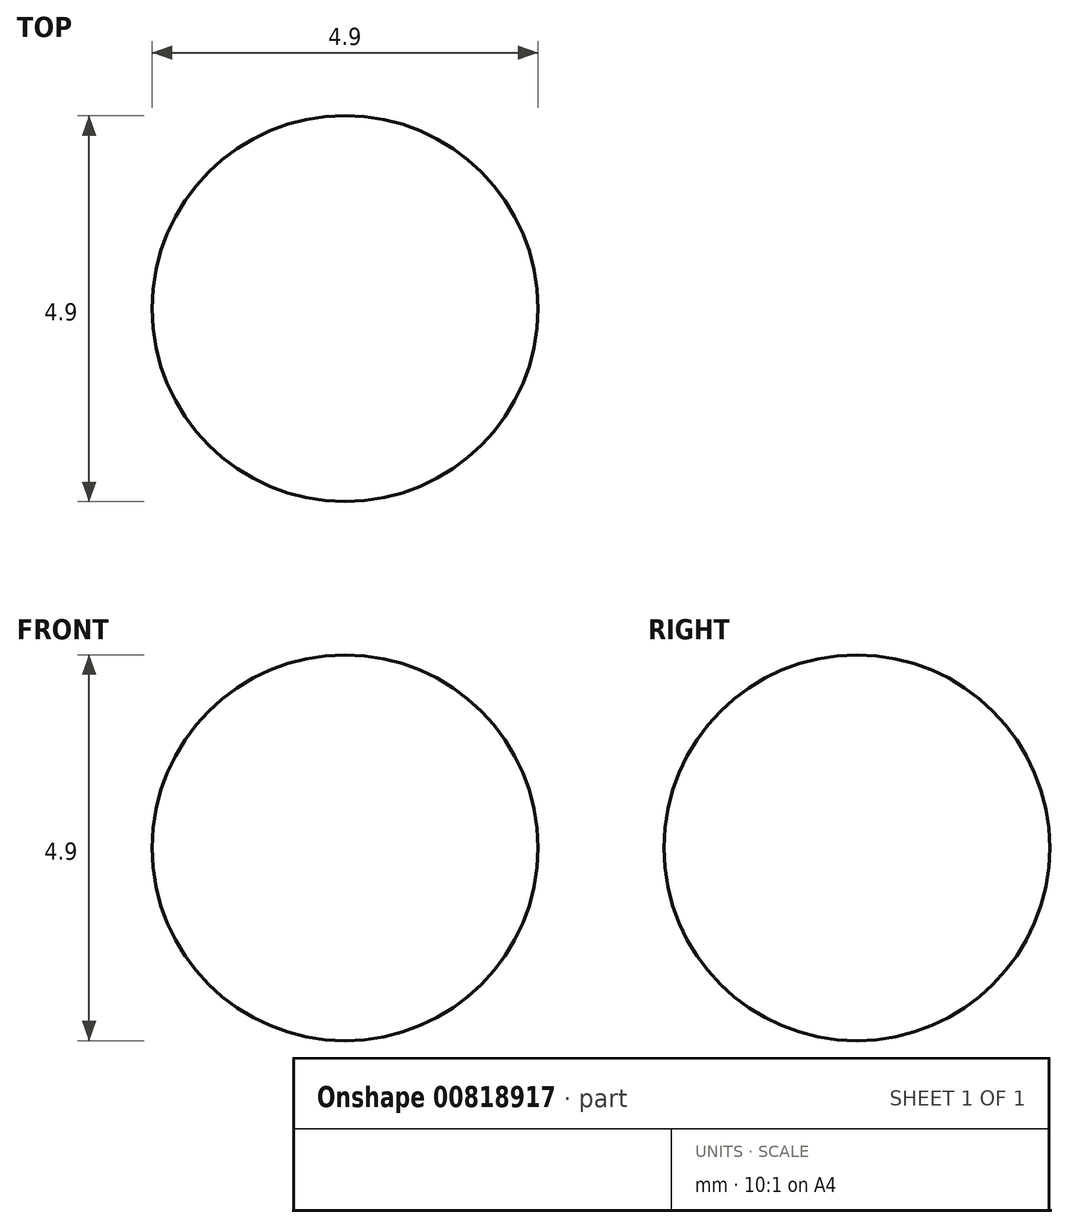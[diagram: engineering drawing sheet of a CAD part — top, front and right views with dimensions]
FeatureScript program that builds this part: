
annotation { "Feature Type Name" : "Feature", "Feature Type Description" : "" }
export const myFeature = defineFeature(function(context is Context, id is Id, definition is map)
    precondition{}
    {
        {
            var Q0;
            Q0=qCreatedBy(makeId("Front.planeOp"),FACE);
            var sketch = newSketch(context, id + "F0", { "sketchPlane" : qUnion([Q0])});
            skArc(sketch, "E0", {"start": v(-2.45, 0) * mm, "mid": v(-1.73, 1.73) * mm, "end": v(0, 2.45) * mm});
            skLineSegment(sketch, "E1", {"start": v(0, 2.45) * mm, "end": v(0, 0) * mm});
            skArc(sketch, "E2", {"start": v(-2.45, 0) * mm, "mid": v(-1.73, -1.73) * mm, "end": v(0, -2.45) * mm});
            skLineSegment(sketch, "E3", {"start": v(0, -2.45) * mm, "end": v(0, 0) * mm});
            skSolve(sketch);
        }
        {
            var Q0;
            Q0 = qSketchRegion(id + "F0", true);
            var Q1;
            Q1=sQuery(id+"F0.wireOp",EDGE,"E1");
            revolve(context, id + "F1", {"surfaceOperationType" : NewSurfaceOperationType.NEW, "entities" : qUnion([Q0]), "axis" : qUnion([Q1]), "revolveType" : RevolveType.FULL});
        }
    });
